# Revit family: Grinder_Pump-Single_Directional-Zoeller-7013_Series
name_source: partatom
category: Mechanical Equipment
units: mm (PartAtom-declared; Revit-internal decimal feet)

## family parameters
Always vertical = No
Cut with Voids When Loaded = No
OmniClass Number = 23.60.30.21
OmniClass Title = Pumps
Part Type = Normal
Room Calculation Point = No
Round Connector Dimension = Use Radius
Shared = Yes
Work Plane-Based = Yes

## types (1)
- E7013/230V/1Ph/60 Hz
    Adapter = Cast Iron
    Amps = 17.2
    Apparent Load = 3956 VA
    Assembly Code = D2010900
    Cap = Cast Iron
    Cord Length = 240"
    Cutter = Hardened Stainless Steel, Rockwell C55-60
    Default Elevation = 0"
    Description = 7013 Grinder Pimp - Single Directional
    Discharge Diameter = 1 1/4" NPT
    Discharge Radius = 5/8"
    Hardware = Stainless Steel 304
    Height = 20 5/8"
    Hertz = 60
    Impeller Diameter = 6 1/8"
    Impeller Type = Ductile Iron
    Installation Type = Floor Mounted
    Length = 10 1/2"
    Lower Bearing = Ball Bearing
    Manufacturer = Zoeller
    Material = Cast Iron-Zoeller-Powder Coated Epoxy
    Max Flow @ 5' = 61 GPM
    Max. Flow at Min. Head = 61GPM @ 5'
    Maximum Head = 1500"
    Mechanical Seals = Dual mechanical shaft seals - upper carbon/ceramic, lower silicon carbide/carbon
    Model = E7013
    Motor = 2 HP
    Motor Housing = Cast Iron
    Motor Shaft = Stainless Steel 416
    Motor Thermal Shutoff = Thermal Overload (1 Ph)
    Motor Type = Submersible
    Nominal Height = 5"
    Operation = Non-Automatic
    Overall Height = 23 3/4"
    Phase = 1
    Price = Prices may vary. Please consult Manufacturer Representative for most up-to-date price list.
    Product Page URL = https://www.zoellerengineered.com
    Pump Housing = Cast Iron
    RPM = 3450
    Shipping Weight = 135 lbs.
    Square Rings = Neoprene
    Type = Capacitor Start/Run
    URL = http://www.zoellerengprod.com
    Upper Bearing = Ball Bearing
    Voltage = 230V
    Warranty Information = 36 Months (Limited)
    Width = 8"

## geometry (parser evidence)
native form markers: Sweep x2
no freeform markers — native parametric forms only
